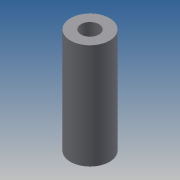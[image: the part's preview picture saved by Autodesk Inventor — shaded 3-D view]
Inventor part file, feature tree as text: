
AUTODESK INVENTOR PART (.ipt)
format: ipt  version: 2013 (Build 170138000, 138)  size: 69,632 bytes
history: native  units: mm
features: extrude x1, sketch x1
ambient origin geometry x8: Origin, YZ Plane, XZ Plane, XY Plane, X Axis, Y Axis, Z Axis, Center Point
bodies: Solid1 (feature_tree)
feature tree (2):
  extrude  "Extrusion1"  Depth=6.0mm
  sketch  "Sketch1"  dims[d0=13.0mm d2=6.0mm d3=35.0mm d4=0.0mm]
